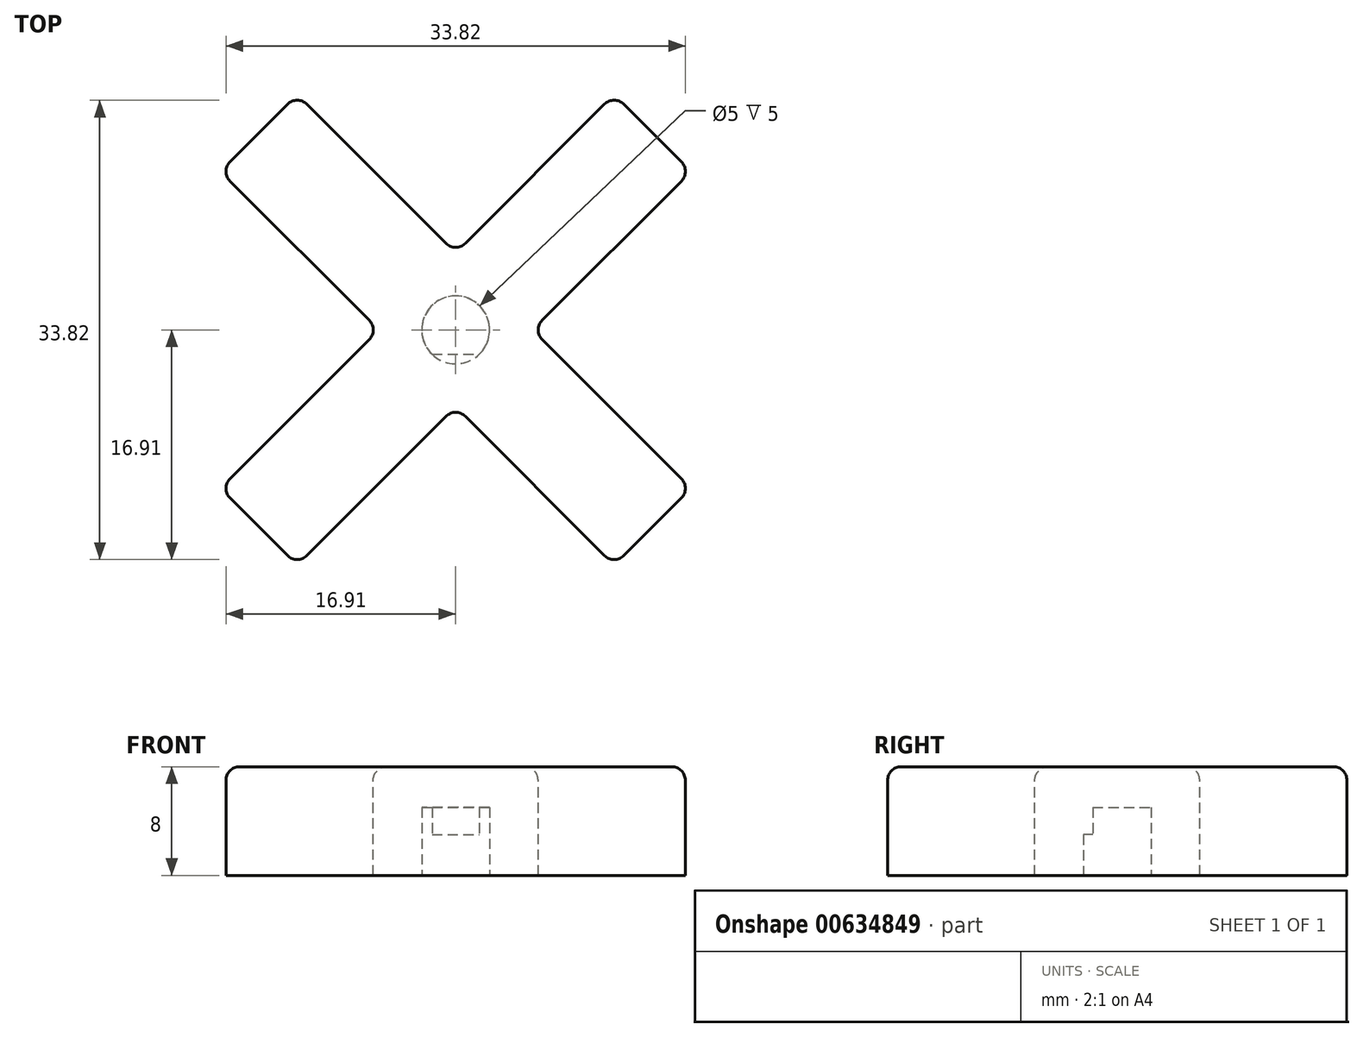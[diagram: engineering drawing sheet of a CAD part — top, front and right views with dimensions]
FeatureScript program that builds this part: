
annotation { "Feature Type Name" : "Feature", "Feature Type Description" : "" }
export const myFeature = defineFeature(function(context is Context, id is Id, definition is map)
    precondition{}
    {
        {
            var Q0;
            Q0=qCreatedBy(makeId("Top.planeOp"),FACE);
            var sketch = newSketch(context, id + "F0", { "sketchPlane" : qUnion([Q0])});
            skLineSegment(sketch, "E0", {"start": v(-17.32, 11.67) * mm, "end": v(-5.66, 0) * mm});
            skLineSegment(sketch, "E1", {"start": v(-5.66, 0) * mm, "end": v(-17.32, -11.67) * mm});
            skLineSegment(sketch, "E2", {"start": v(-17.32, -11.67) * mm, "end": v(-11.67, -17.32) * mm});
            skLineSegment(sketch, "E3", {"start": v(-11.67, -17.32) * mm, "end": v(0, -5.66) * mm});
            skLineSegment(sketch, "E4", {"start": v(0, -5.66) * mm, "end": v(11.67, -17.32) * mm});
            skLineSegment(sketch, "E5", {"start": v(11.67, -17.32) * mm, "end": v(17.32, -11.67) * mm});
            skLineSegment(sketch, "E6", {"start": v(17.32, -11.67) * mm, "end": v(5.66, 0) * mm});
            skLineSegment(sketch, "E7", {"start": v(5.66, 0) * mm, "end": v(17.32, 11.67) * mm});
            skLineSegment(sketch, "E8", {"start": v(17.32, 11.67) * mm, "end": v(11.67, 17.32) * mm});
            skLineSegment(sketch, "E9", {"start": v(11.67, 17.32) * mm, "end": v(0, 5.66) * mm});
            skLineSegment(sketch, "E10", {"start": v(0, 5.66) * mm, "end": v(-11.67, 17.32) * mm});
            skLineSegment(sketch, "E11", {"start": v(-11.67, 17.32) * mm, "end": v(-17.32, 11.67) * mm});
            skCircle(sketch, "E12.cCircle", {"center": v(0, 0) * mm, "radius": 4 * mm, "construction": true});
            skLineSegment(sketch, "E12.0", {"start": v(0, 5.66) * mm, "end": v(5.66, 0) * mm, "construction": true});
            skLineSegment(sketch, "E12.1", {"start": v(5.66, 0) * mm, "end": v(0, -5.66) * mm, "construction": true});
            skLineSegment(sketch, "E12.2", {"start": v(0, -5.66) * mm, "end": v(-5.66, 0) * mm, "construction": true});
            skLineSegment(sketch, "E12.3", {"start": v(-5.66, 0) * mm, "end": v(0, 5.66) * mm, "construction": true});
            skPoint(sketch, "E12.0.midPoint", {"position": v(2.83, 2.83) * mm});
            skCircle(sketch, "E13", {"center": v(0, 0) * mm, "radius": 2.5 * mm});
            skLineSegment(sketch, "E14", {"start": v(-1.73, -1.8) * mm, "end": v(1.73, -1.8) * mm});
            skLineSegment(sketch, "E15", {"start": v(0, 0) * mm, "end": v(0, -2.5) * mm, "construction": true});
            skSolve(sketch);
        }
        {
            var Q0;
            Q0=makeQuery(id+"F0.imprint","IMPRINT",FACE,{"disambiguationData":[TD([[makeQuery(id+"F0.imprint","IMPRINT",EDGE,{"derivedFrom":sQuery(id+"F0.wireOp",EDGE,"E7")}),1.0]])]});
            var Q1;
            Q1=makeQuery(id+"F0.imprint","IMPRINT",FACE,{"disambiguationData":[TD([[makeQuery(id+"F0.imprint","IMPRINT",EDGE,{"derivedFrom":sQuery(id+"F0.wireOp",EDGE,"E4")}),1.0]])]});
            var Q2;
            Q2=makeQuery(id+"F0.imprint","IMPRINT",FACE,{"disambiguationData":[TD([[makeQuery(id+"F0.imprint","IMPRINT",EDGE,{"derivedFrom":sQuery(id+"F0.wireOp",EDGE,"E12.0")}),-1.0]])]});
            var Q3;
            Q3=makeQuery(id+"F0.imprint","IMPRINT",FACE,{"disambiguationData":[TD([[makeQuery(id+"F0.imprint","IMPRINT",EDGE,{"derivedFrom":sQuery(id+"F0.wireOp",EDGE,"E0")}),1.0]])]});
            var Q4;
            Q4=makeQuery(id+"F0.imprint","IMPRINT",FACE,{"disambiguationData":[TD([[makeQuery(id+"F0.imprint","IMPRINT",EDGE,{"derivedFrom":sQuery(id+"F0.wireOp",EDGE,"E1")}),1.0]])]});
            var Q5;
            Q5=makeQuery(id+"F0.imprint","IMPRINT",FACE,{"disambiguationData":[TD([[makeQuery(id+"F0.imprint","IMPRINT",EDGE,{"derivedFrom":sQuery(id+"F0.wireOp",EDGE,"E13")}),1.0]])]});
            extrude(context, id + "F1", {"entities" : qUnion([Q0, Q1, Q2, Q3, Q4, Q5]), "depth" : 8 * mm, "offsetDistance" : 25 * mm});
        }
        {
            var Q0;
            Q0=makeQuery(id+"F1.opExtrude","CAP_FACE",FACE,{"disambiguationData":[OSD([sQuery(id+"F0.wireOp",EDGE,"E0"),sQuery(id+"F0.wireOp",EDGE,"E1"),sQuery(id+"F0.wireOp",EDGE,"E2"),sQuery(id+"F0.wireOp",EDGE,"E3"),sQuery(id+"F0.wireOp",EDGE,"E4"),sQuery(id+"F0.wireOp",EDGE,"E5"),sQuery(id+"F0.wireOp",EDGE,"E6"),sQuery(id+"F0.wireOp",EDGE,"E7"),sQuery(id+"F0.wireOp",EDGE,"E8"),sQuery(id+"F0.wireOp",EDGE,"E9"),sQuery(id+"F0.wireOp",EDGE,"E10"),sQuery(id+"F0.wireOp",EDGE,"E11")])],"isStart":false});
            var Q1;
            Q1=makeQuery(id+"F1.opExtrude","SWEPT_EDGE",EDGE,{"disambiguationData":[OSD([sQuery(id+"F0.wireOp",EDGE,"E2"),sQuery(id+"F0.wireOp",EDGE,"E3")])]});
            var Q2;
            Q2=makeQuery(id+"F1.opExtrude","SWEPT_EDGE",EDGE,{"disambiguationData":[OSD([sQuery(id+"F0.wireOp",EDGE,"E1"),sQuery(id+"F0.wireOp",EDGE,"E2")])]});
            var Q3;
            Q3=makeQuery(id+"F1.opExtrude","SWEPT_EDGE",EDGE,{"disambiguationData":[OSD([sQuery(id+"F0.wireOp",EDGE,"E0"),sQuery(id+"F0.wireOp",EDGE,"E11")])]});
            var Q4;
            Q4=makeQuery(id+"F1.opExtrude","SWEPT_EDGE",EDGE,{"disambiguationData":[OSD([sQuery(id+"F0.wireOp",EDGE,"E4"),sQuery(id+"F0.wireOp",EDGE,"E5")])]});
            var Q5;
            Q5=makeQuery(id+"F1.opExtrude","SWEPT_EDGE",EDGE,{"disambiguationData":[OSD([sQuery(id+"F0.wireOp",EDGE,"E5"),sQuery(id+"F0.wireOp",EDGE,"E6")])]});
            var Q6;
            Q6=makeQuery(id+"F1.opExtrude","SWEPT_EDGE",EDGE,{"disambiguationData":[OSD([sQuery(id+"F0.wireOp",EDGE,"E7"),sQuery(id+"F0.wireOp",EDGE,"E8")])]});
            var Q7;
            Q7=makeQuery(id+"F1.opExtrude","SWEPT_EDGE",EDGE,{"disambiguationData":[OSD([sQuery(id+"F0.wireOp",EDGE,"E8"),sQuery(id+"F0.wireOp",EDGE,"E9")])]});
            var Q8;
            Q8=makeQuery(id+"F1.opExtrude","SWEPT_EDGE",EDGE,{"disambiguationData":[OSD([sQuery(id+"F0.wireOp",EDGE,"E10"),sQuery(id+"F0.wireOp",EDGE,"E11")])]});
            var Q9;
            Q9=makeQuery(id+"F1.opExtrude","SWEPT_EDGE",EDGE,{"disambiguationData":[OSD([sQuery(id+"F0.wireOp",EDGE,"E9"),sQuery(id+"F0.wireOp",EDGE,"E10"),sQuery(id+"F0.wireOp",EDGE,"E12.0"),sQuery(id+"F0.wireOp",EDGE,"E12.3")])]});
            var Q10;
            Q10=makeQuery(id+"F1.opExtrude","SWEPT_EDGE",EDGE,{"disambiguationData":[OSD([sQuery(id+"F0.wireOp",EDGE,"E0"),sQuery(id+"F0.wireOp",EDGE,"E1"),sQuery(id+"F0.wireOp",EDGE,"E12.2"),sQuery(id+"F0.wireOp",EDGE,"E12.3")])]});
            var Q11;
            Q11=makeQuery(id+"F1.opExtrude","SWEPT_EDGE",EDGE,{"disambiguationData":[OSD([sQuery(id+"F0.wireOp",EDGE,"E3"),sQuery(id+"F0.wireOp",EDGE,"E4"),sQuery(id+"F0.wireOp",EDGE,"E12.1"),sQuery(id+"F0.wireOp",EDGE,"E12.2")])]});
            var Q12;
            Q12=makeQuery(id+"F1.opExtrude","SWEPT_EDGE",EDGE,{"disambiguationData":[OSD([sQuery(id+"F0.wireOp",EDGE,"E6"),sQuery(id+"F0.wireOp",EDGE,"E7"),sQuery(id+"F0.wireOp",EDGE,"E12.0"),sQuery(id+"F0.wireOp",EDGE,"E12.1")])]});
            fillet(context, id + "F2", {"entities" : qUnion([Q0, Q1, Q2, Q3, Q4, Q5, Q6, Q7, Q8, Q9, Q10, Q11, Q12]), "radius" : 1 * mm, "tangentPropagation" : true, "allowEdgeOverflow" : false});
        }
        {
            var Q0;
            {var subQ0=sQuery(id+"F0.wireOp",EDGE,"E14");Q0=makeQuery(id+"F0.imprint","IMPRINT",FACE,{"disambiguationData":[TD([[makeQuery(id+"F0.imprint","IMPRINT",EDGE,{"derivedFrom":subQ0}),1.0]])]});}
            extrude(context, id + "F3", {"entities" : qUnion([Q0]), "operationType" : NewBodyOperationType.REMOVE, "depth" : 5 * mm, "offsetDistance" : 25 * mm});
        }
        {
            var Q0;
            {var subQ0=sQuery(id+"F0.wireOp",EDGE,"E14");Q0=makeQuery(id+"F0.imprint","IMPRINT",FACE,{"disambiguationData":[TD([[makeQuery(id+"F0.imprint","IMPRINT",EDGE,{"derivedFrom":subQ0}),-1.0]])]});}
            extrude(context, id + "F4", {"entities" : qUnion([Q0]), "operationType" : NewBodyOperationType.REMOVE, "depth" : 3 * mm, "offsetDistance" : 25 * mm});
        }
    });
